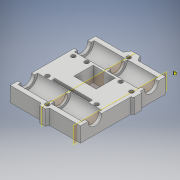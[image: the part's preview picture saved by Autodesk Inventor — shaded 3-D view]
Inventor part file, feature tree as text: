
AUTODESK INVENTOR PART (.ipt)
format: ipt  version: 2018 (Build 220112000, 112)  size: 305,152 bytes
history: native  units: mm
features: extrude x7, sketch x7, plane x2, mirror x1
ambient origin geometry x8: Origin, YZ Plane, XZ Plane, XY Plane, X Axis, Y Axis, Z Axis, Center Point
bodies: Solid1 (feature_tree)
feature tree (17):
  extrude  "Extrusion1"  Depth=68.0mm
  extrude  "Extrusion2"  Depth=12.0mm
  plane  "Work Plane1"
  extrude  "Extrusion3"  Depth=11.0mm
  plane  "Work Plane2"
  mirror  "Mirror1"
  extrude  "Extrusion9"  Depth=15.7mm
  extrude  "Extrusion11"  [1 undecoded]
  extrude  "Extrusion12"  [1 undecoded]
  sketch  "Sketch14"  dims[d21=1.6mm d82=2.0mm d83=1.5mm d84=1.5mm d93=10.0mm d94=0.0mm d105=15.3mm d116=2.6mm d117=30.0mm d118=4.65mm d119=3.3mm d121=3.3mm d122=4.65mm d123=3.3mm d124=3.3mm d125=3.3mm d126=0.5mm d127=0.0mm d128=0.0mm d131=1.749395mm d133=7.0mm d134=0.0mm d138=6.0mm d139=6.0mm d140=6.0mm d141=6.0mm d142=10.0mm d150=3.1mm d151=0.0mm d152=0.651024mm]
  extrude  "Extrusion13"  Depth=2.0mm
  sketch  "Sketch1"  dims[d0=56.0mm d1=68.0mm]
  sketch  "Sketch2"  dims[d2=12.0mm d3=0.0mm d4=22.5mm]
  sketch  "Sketch3"  dims[d5=11.0mm d6=11.0mm]
  sketch  "Sketch10"  dims[d7=0.0mm d8=0.0mm d9=15.7mm]
  sketch  "Sketch12"  dims[d10=15.7mm d11=-2.5mm]
  sketch  "Sketch13"  dims[d12=24.5mm d13=0.0mm d14=-28.0mm]
note: 2 required parameter values undecoded (feature->parameter linkage not recoverable at this tier; creation-order binding heuristic only, values carry confidence <= 0.55)
